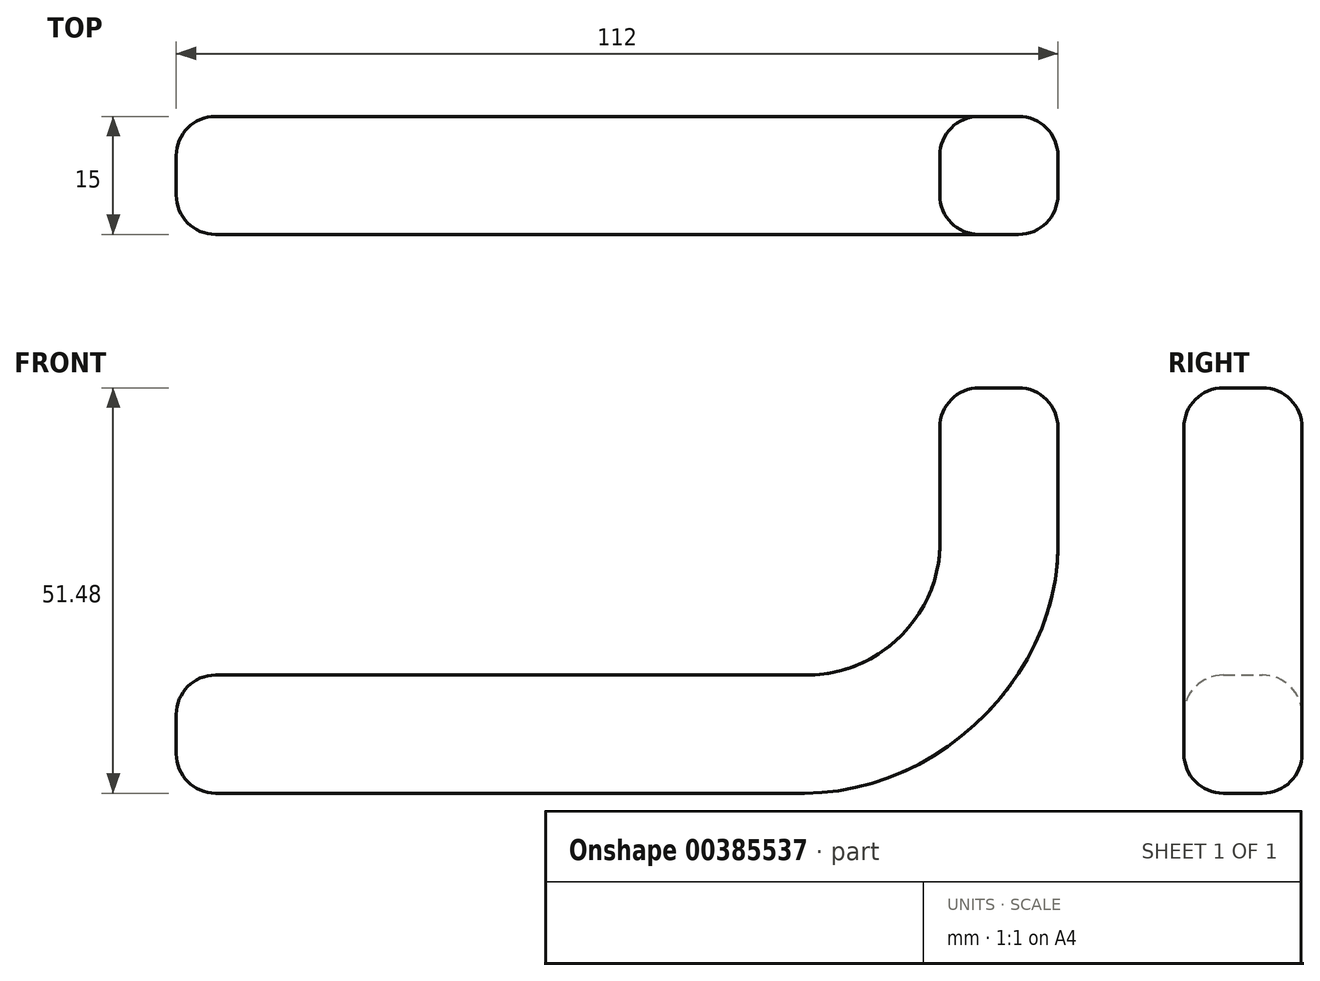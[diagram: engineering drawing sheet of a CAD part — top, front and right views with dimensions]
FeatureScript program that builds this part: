
annotation { "Feature Type Name" : "Feature", "Feature Type Description" : "" }
export const myFeature = defineFeature(function(context is Context, id is Id, definition is map)
    precondition{}
    {
        {
            var Q0;
            Q0=qCreatedBy(makeId("Front.planeOp"),FACE);
            var sketch = newSketch(context, id + "F0", { "sketchPlane" : qUnion([Q0])});
            skLineSegment(sketch, "E0", {"start": v(0, 15) * mm, "end": v(80, 15) * mm});
            skLineSegment(sketch, "E1.1", {"start": v(-0.18, 0) * mm, "end": v(79.82, 0) * mm});
            skLineSegment(sketch, "E2.bottom", {"start": v(97, 31.48) * mm, "end": v(112, 31.48) * mm});
            skLineSegment(sketch, "E2.top", {"start": v(97, 51.48) * mm, "end": v(112, 51.48) * mm});
            skLineSegment(sketch, "E2.left", {"start": v(97, 31.48) * mm, "end": v(97, 51.48) * mm});
            skLineSegment(sketch, "E2.right", {"start": v(112, 31.48) * mm, "end": v(112, 51.48) * mm});
            skFitSpline(sketch, "E3", {"points": [v(80, 15) * mm, v(97, 31.48) * mm], "startDerivative": vector(30.17, 0) * mm, "endDerivative": vector(0, 24.3) * mm});
            skFitSpline(sketch, "E4", {"points": [v(112, 31.48) * mm, v(79.82, 0) * mm], "startDerivative": vector(0, -49.43) * mm, "endDerivative": vector(-51.52, 0) * mm});
            skLineSegment(sketch, "E5", {"start": v(80, 15) * mm, "end": v(79.82, 0) * mm});
            skLineSegment(sketch, "E6", {"start": v(0, 15) * mm, "end": v(-0.18, 0) * mm});
            skLineSegment(sketch, "E7.left", {"start": v(0, 15) * mm, "end": v(0, 0) * mm});
            skSolve(sketch);
        }
        {
            var Q0;
            Q0=makeQuery(id+"F0.imprint","IMPRINT",FACE,{"disambiguationData":[TD([[makeQuery(id+"F0.imprint","IMPRINT",EDGE,{"derivedFrom":sQuery(id+"F0.wireOp",EDGE,"meLjfQBB-0KZx-YIKJ-ggGc-JeM5xshYHCOn.bottom")}),-1.0]])]});
            var Q1;
            Q1=makeQuery(id+"F0.imprint","IMPRINT",FACE,{"disambiguationData":[TD([[makeQuery(id+"F0.imprint","IMPRINT",EDGE,{"derivedFrom":sQuery(id+"F0.wireOp",EDGE,"meLjfQBB-0KZx-YIKJ-ggGc-JeM5xshYHCOn.right")}),1.0]])]});
            var Q2;
            Q2=makeQuery(id+"F0.imprint","IMPRINT",FACE,{"disambiguationData":[TD([[makeQuery(id+"F0.imprint","IMPRINT",EDGE,{"derivedFrom":sQuery(id+"F0.wireOp",EDGE,"E2.bottom")}),-1.0]])]});
            var Q3;
            Q3=makeQuery(id+"F0.imprint","IMPRINT",FACE,{"disambiguationData":[TD([[makeQuery(id+"F0.imprint","IMPRINT",EDGE,{"derivedFrom":sQuery(id+"F0.wireOp",EDGE,"E2.bottom")}),1.0]])]});
            var Q4;
            Q4=makeQuery(id+"F0.imprint","IMPRINT",FACE,{"disambiguationData":[TD([[makeQuery(id+"F0.imprint","IMPRINT",EDGE,{"derivedFrom":sQuery(id+"F0.wireOp",EDGE,"E0")}),-1.0]])]});
            var Q5;
            Q5=makeQuery(id+"F0.imprint","IMPRINT",FACE,{"disambiguationData":[TD([[makeQuery(id+"F0.imprint","IMPRINT",EDGE,{"derivedFrom":sQuery(id+"F0.wireOp",EDGE,"E7.bottom")}),1.0]])]});
            extrude(context, id + "F1", {"entities" : qUnion([Q0, Q1, Q2, Q3, Q4, Q5]), "depth" : 15 * mm});
        }
        {
            var Q0;
            Q0=makeQuery(id+"F1.opExtrude","SWEPT_FACE",FACE,{"disambiguationData":[OSD([sQuery(id+"F0.wireOp",EDGE,"E0"),sQuery(id+"F0.wireOp",EDGE,"E7.bottom")])]});
            var Q1;
            Q1=makeQuery(id+"F1.opExtrude","SWEPT_FACE",FACE,{"disambiguationData":[OSD([sQuery(id+"F0.wireOp",EDGE,"E2.top")])]});
            var Q2;
            Q2=makeQuery(id+"F1.opExtrude","CAP_FACE",FACE,{"disambiguationData":[OSD([sQuery(id+"F0.wireOp",EDGE,"E0"),sQuery(id+"F0.wireOp",EDGE,"E1.1"),sQuery(id+"F0.wireOp",EDGE,"E2.top"),sQuery(id+"F0.wireOp",EDGE,"E2.left"),sQuery(id+"F0.wireOp",EDGE,"E2.right"),sQuery(id+"F0.wireOp",EDGE,"E3"),sQuery(id+"F0.wireOp",EDGE,"E4"),sQuery(id+"F0.wireOp",EDGE,"E7.bottom"),sQuery(id+"F0.wireOp",EDGE,"E7.top"),sQuery(id+"F0.wireOp",EDGE,"E7.right")])],"isStart":false});
            var Q3;
            Q3=makeQuery(id+"F1.opExtrude","SWEPT_FACE",FACE,{"disambiguationData":[OSD([sQuery(id+"F0.wireOp",EDGE,"E2.right")])]});
            var Q4;
            Q4=makeQuery(id+"F1.opExtrude","SWEPT_FACE",FACE,{"disambiguationData":[OSD([sQuery(id+"F0.wireOp",EDGE,"E4")])]});
            var Q5;
            Q5=makeQuery(id+"F1.opExtrude","SWEPT_FACE",FACE,{"disambiguationData":[OSD([sQuery(id+"F0.wireOp",EDGE,"E1.1"),sQuery(id+"F0.wireOp",EDGE,"E7.top")])]});
            fillet(context, id + "F2", {"entities" : qUnion([Q0, Q1, Q2, Q3, Q4, Q5]), "radius" : 5 * mm, "tangentPropagation" : true, "allowEdgeOverflow" : false});
        }
        {
            var Q0;
            Q0=makeQuery(id+"F1.opExtrude","SWEPT_FACE",FACE,{"disambiguationData":[OSD([sQuery(id+"F0.wireOp",EDGE,"E1.1")])]});
            var Q1;
            {var subQ0=sQuery(id+"F0.wireOp",EDGE,"E1.1");Q1=makeQuery(id+"F2.opFillet","BLEND_FACE",FACE,{"disambiguationData":[OSD([subQ0]),TDD([makeQuery(id+"F1.opExtrude","CAP_EDGE",EDGE,{"disambiguationData":[OSD([subQ0])],"isStart":false})])]});}
            var Q2;
            {var subQ0=sQuery(id+"F0.wireOp",EDGE,"E1.1");Q2=makeQuery(id+"F2.opFillet","BLEND_FACE",FACE,{"disambiguationData":[OSD([subQ0]),TDD([makeQuery(id+"F1.opExtrude","CAP_EDGE",EDGE,{"disambiguationData":[OSD([subQ0])],"isStart":true})])]});}
            var Q3;
            {var subQ0=sQuery(id+"F0.wireOp",EDGE,"E7.left");var subQ1=sQuery(id+"F0.wireOp",EDGE,"E6");var subQ2=sQuery(id+"F0.wireOp",EDGE,"E0");Q3=makeQuery(id+"F2.opFillet","BLEND_FACE",FACE,{"disambiguationData":[OSD([subQ2,subQ1,subQ0]),TDD([makeQuery(id+"F1.opExtrude","SWEPT_EDGE",EDGE,{"disambiguationData":[OSD([subQ2,subQ1,subQ0])]})])]});}
            var Q4;
            {var subQ0=sQuery(id+"F0.wireOp",EDGE,"E7.left");var subQ1=sQuery(id+"F0.wireOp",EDGE,"E1.1");Q4=makeQuery(id+"F2.opFillet","BLEND_FACE",FACE,{"disambiguationData":[OSD([subQ1,subQ0]),TDD([makeQuery(id+"F1.opExtrude","CAP_VERTEX",VERTEX,{"disambiguationData":[OSD([subQ1,subQ0])],"isStart":false})])]});}
            var Q5;
            Q5=makeQuery(id+"F2.opFillet","BLEND_FACE",FACE,{"disambiguationData":[OSD([sQuery(id+"F0.wireOp",EDGE,"E7.left")])]});
            var Q6;
            {var subQ0=sQuery(id+"F0.wireOp",EDGE,"E7.left");Q6=makeQuery(id+"F2.opFillet","BLEND_EDGE",EDGE,{"blendedFrom":[makeQuery(id+"F1.opExtrude","SWEPT_EDGE",EDGE,{"disambiguationData":[OSD([sQuery(id+"F0.wireOp",EDGE,"E0"),sQuery(id+"F0.wireOp",EDGE,"E6"),subQ0])]}),makeQuery(id+"F1.opExtrude","SWEPT_FACE",FACE,{"disambiguationData":[OSD([subQ0])]})],"blendedInto":[makeQuery(id+"F1.opExtrude","SWEPT_FACE",FACE,{"disambiguationData":[OSD([subQ0])]})]});}
            var Q7;
            {var subQ0=sQuery(id+"F0.wireOp",EDGE,"E0");Q7=makeQuery(id+"F2.opFillet","BLEND_FACE",FACE,{"disambiguationData":[OSD([subQ0]),TDD([makeQuery(id+"F1.opExtrude","CAP_EDGE",EDGE,{"disambiguationData":[OSD([subQ0])],"isStart":true})])]});}
            var Q8;
            {var subQ0=sQuery(id+"F0.wireOp",EDGE,"E0");Q8=makeQuery(id+"F2.opFillet","BLEND_EDGE",EDGE,{"blendedFrom":[makeQuery(id+"F1.opExtrude","CAP_EDGE",EDGE,{"disambiguationData":[OSD([subQ0])],"isStart":true}),makeQuery(id+"F1.opExtrude","SWEPT_FACE",FACE,{"disambiguationData":[OSD([subQ0])]})],"blendedInto":[makeQuery(id+"F1.opExtrude","SWEPT_FACE",FACE,{"disambiguationData":[OSD([subQ0])]})]});}
            var Q9;
            Q9=makeQuery(id+"F1.opExtrude","SWEPT_FACE",FACE,{"disambiguationData":[OSD([sQuery(id+"F0.wireOp",EDGE,"E0")])]});
            var Q10;
            {var subQ0=sQuery(id+"F0.wireOp",EDGE,"E0");Q10=makeQuery(id+"F2.opFillet","BLEND_FACE",FACE,{"disambiguationData":[OSD([subQ0]),TDD([makeQuery(id+"F1.opExtrude","CAP_EDGE",EDGE,{"disambiguationData":[OSD([subQ0])],"isStart":false})])]});}
            var Q11;
            {var subQ0=sQuery(id+"F0.wireOp",EDGE,"E3");Q11=makeQuery(id+"F2.opFillet","BLEND_FACE",FACE,{"disambiguationData":[OSD([subQ0]),TDD([makeQuery(id+"F1.opExtrude","CAP_EDGE",EDGE,{"disambiguationData":[OSD([subQ0])],"isStart":false})])]});}
            var Q12;
            Q12=makeQuery(id+"F1.opExtrude","CAP_FACE",FACE,{"disambiguationData":[OSD([sQuery(id+"F0.wireOp",EDGE,"E0"),sQuery(id+"F0.wireOp",EDGE,"E1.1"),sQuery(id+"F0.wireOp",EDGE,"E2.top"),sQuery(id+"F0.wireOp",EDGE,"E2.left"),sQuery(id+"F0.wireOp",EDGE,"E2.right"),sQuery(id+"F0.wireOp",EDGE,"E3"),sQuery(id+"F0.wireOp",EDGE,"E4"),sQuery(id+"F0.wireOp",EDGE,"E7.left")])],"isStart":false});
            var Q13;
            {var subQ0=sQuery(id+"F0.wireOp",EDGE,"E4");Q13=makeQuery(id+"F2.opFillet","BLEND_FACE",FACE,{"disambiguationData":[OSD([subQ0]),TDD([makeQuery(id+"F1.opExtrude","CAP_EDGE",EDGE,{"disambiguationData":[OSD([subQ0])],"isStart":false})])]});}
            var Q14;
            {var subQ0=sQuery(id+"F0.wireOp",EDGE,"E2.right");Q14=makeQuery(id+"F2.opFillet","BLEND_FACE",FACE,{"disambiguationData":[OSD([subQ0]),TDD([makeQuery(id+"F1.opExtrude","CAP_EDGE",EDGE,{"disambiguationData":[OSD([subQ0])],"isStart":false})])]});}
            var Q15;
            {var subQ0=sQuery(id+"F0.wireOp",EDGE,"E2.left");Q15=makeQuery(id+"F2.opFillet","BLEND_FACE",FACE,{"disambiguationData":[OSD([subQ0]),TDD([makeQuery(id+"F1.opExtrude","CAP_EDGE",EDGE,{"disambiguationData":[OSD([subQ0])],"isStart":false})])]});}
            var Q16;
            {var subQ0=sQuery(id+"F0.wireOp",EDGE,"E2.top");Q16=makeQuery(id+"F2.opFillet","BLEND_EDGE",EDGE,{"blendedFrom":[makeQuery(id+"F1.opExtrude","CAP_VERTEX",VERTEX,{"disambiguationData":[OSD([subQ0,sQuery(id+"F0.wireOp",EDGE,"E2.left")])],"isStart":false}),makeQuery(id+"F1.opExtrude","CAP_EDGE",EDGE,{"disambiguationData":[OSD([subQ0])],"isStart":false})],"blendedInto":[]});}
            var Q17;
            {var subQ0=sQuery(id+"F0.wireOp",EDGE,"E2.top");Q17=makeQuery(id+"F2.opFillet","BLEND_FACE",FACE,{"disambiguationData":[OSD([subQ0]),TDD([makeQuery(id+"F1.opExtrude","CAP_EDGE",EDGE,{"disambiguationData":[OSD([subQ0])],"isStart":false})])]});}
            var Q18;
            {var subQ0=sQuery(id+"F0.wireOp",EDGE,"E2.right");var subQ1=sQuery(id+"F0.wireOp",EDGE,"E2.top");Q18=makeQuery(id+"F2.opFillet","BLEND_FACE",FACE,{"disambiguationData":[OSD([subQ1,subQ0]),TDD([makeQuery(id+"F1.opExtrude","CAP_VERTEX",VERTEX,{"disambiguationData":[OSD([subQ1,subQ0])],"isStart":false})])]});}
            var Q19;
            {var subQ0=sQuery(id+"F0.wireOp",EDGE,"E3");Q19=makeQuery(id+"F2.opFillet","BLEND_FACE",FACE,{"disambiguationData":[OSD([subQ0]),TDD([makeQuery(id+"F1.opExtrude","CAP_EDGE",EDGE,{"disambiguationData":[OSD([subQ0])],"isStart":true})])]});}
            var Q20;
            Q20=makeQuery(id+"F1.opExtrude","SWEPT_FACE",FACE,{"disambiguationData":[OSD([sQuery(id+"F0.wireOp",EDGE,"E3")])]});
            var Q21;
            {var subQ0=sQuery(id+"F0.wireOp",EDGE,"E4");Q21=makeQuery(id+"F2.opFillet","BLEND_EDGE",EDGE,{"blendedFrom":[makeQuery(id+"F1.opExtrude","CAP_EDGE",EDGE,{"disambiguationData":[OSD([subQ0])],"isStart":true}),makeQuery(id+"F1.opExtrude","CAP_FACE",FACE,{"disambiguationData":[OSD([sQuery(id+"F0.wireOp",EDGE,"E0"),sQuery(id+"F0.wireOp",EDGE,"E1.1"),sQuery(id+"F0.wireOp",EDGE,"E2.top"),sQuery(id+"F0.wireOp",EDGE,"E2.left"),sQuery(id+"F0.wireOp",EDGE,"E2.right"),sQuery(id+"F0.wireOp",EDGE,"E3"),subQ0,sQuery(id+"F0.wireOp",EDGE,"E7.left")])],"isStart":true})],"blendedInto":[makeQuery(id+"F1.opExtrude","CAP_FACE",FACE,{"disambiguationData":[OSD([sQuery(id+"F0.wireOp",EDGE,"E0"),sQuery(id+"F0.wireOp",EDGE,"E1.1"),sQuery(id+"F0.wireOp",EDGE,"E2.top"),sQuery(id+"F0.wireOp",EDGE,"E2.left"),sQuery(id+"F0.wireOp",EDGE,"E2.right"),sQuery(id+"F0.wireOp",EDGE,"E3"),subQ0,sQuery(id+"F0.wireOp",EDGE,"E7.left")])],"isStart":true})]});}
            var Q22;
            Q22=makeQuery(id+"F1.opExtrude","CAP_FACE",FACE,{"disambiguationData":[OSD([sQuery(id+"F0.wireOp",EDGE,"E0"),sQuery(id+"F0.wireOp",EDGE,"E1.1"),sQuery(id+"F0.wireOp",EDGE,"E2.top"),sQuery(id+"F0.wireOp",EDGE,"E2.left"),sQuery(id+"F0.wireOp",EDGE,"E2.right"),sQuery(id+"F0.wireOp",EDGE,"E3"),sQuery(id+"F0.wireOp",EDGE,"E4"),sQuery(id+"F0.wireOp",EDGE,"E7.left")])],"isStart":true});
            var Q23;
            {var subQ0=sQuery(id+"F0.wireOp",EDGE,"E2.left");Q23=makeQuery(id+"F2.opFillet","BLEND_FACE",FACE,{"disambiguationData":[OSD([subQ0]),TDD([makeQuery(id+"F1.opExtrude","CAP_EDGE",EDGE,{"disambiguationData":[OSD([subQ0])],"isStart":true})])]});}
            var Q24;
            {var subQ0=sQuery(id+"F0.wireOp",EDGE,"E2.left");var subQ1=sQuery(id+"F0.wireOp",EDGE,"E2.top");Q24=makeQuery(id+"F2.opFillet","BLEND_FACE",FACE,{"disambiguationData":[OSD([subQ1,subQ0]),TDD([makeQuery(id+"F1.opExtrude","CAP_VERTEX",VERTEX,{"disambiguationData":[OSD([subQ1,subQ0])],"isStart":true})])]});}
            var Q25;
            {var subQ0=sQuery(id+"F0.wireOp",EDGE,"E2.left");var subQ1=sQuery(id+"F0.wireOp",EDGE,"E2.top");Q25=makeQuery(id+"F2.opFillet","BLEND_FACE",FACE,{"disambiguationData":[OSD([subQ1,subQ0]),TDD([makeQuery(id+"F1.opExtrude","SWEPT_EDGE",EDGE,{"disambiguationData":[OSD([subQ1,subQ0])]})])]});}
            var Q26;
            {var subQ0=sQuery(id+"F0.wireOp",EDGE,"E2.left");var subQ1=sQuery(id+"F0.wireOp",EDGE,"E2.top");Q26=makeQuery(id+"F2.opFillet","BLEND_EDGE",EDGE,{"blendedFrom":[makeQuery(id+"F1.opExtrude","CAP_VERTEX",VERTEX,{"disambiguationData":[OSD([subQ1,subQ0])],"isStart":false}),makeQuery(id+"F1.opExtrude","SWEPT_EDGE",EDGE,{"disambiguationData":[OSD([subQ1,subQ0])]})],"blendedInto":[]});}
            var Q27;
            {var subQ0=sQuery(id+"F0.wireOp",EDGE,"E2.top");Q27=makeQuery(id+"F2.opFillet","BLEND_FACE",FACE,{"disambiguationData":[OSD([subQ0]),TDD([makeQuery(id+"F1.opExtrude","CAP_EDGE",EDGE,{"disambiguationData":[OSD([subQ0])],"isStart":true})])]});}
            var Q28;
            Q28=makeQuery(id+"F1.opExtrude","SWEPT_FACE",FACE,{"disambiguationData":[OSD([sQuery(id+"F0.wireOp",EDGE,"E2.top")])]});
            var Q29;
            {var subQ0=sQuery(id+"F0.wireOp",EDGE,"E2.right");var subQ1=sQuery(id+"F0.wireOp",EDGE,"E2.top");Q29=makeQuery(id+"F2.opFillet","BLEND_FACE",FACE,{"disambiguationData":[OSD([subQ1,subQ0]),TDD([makeQuery(id+"F1.opExtrude","SWEPT_EDGE",EDGE,{"disambiguationData":[OSD([subQ1,subQ0])]})])]});}
            var Q30;
            {var subQ0=sQuery(id+"F0.wireOp",EDGE,"E2.right");var subQ1=sQuery(id+"F0.wireOp",EDGE,"E2.top");Q30=makeQuery(id+"F2.opFillet","BLEND_FACE",FACE,{"disambiguationData":[OSD([subQ1,subQ0]),TDD([makeQuery(id+"F1.opExtrude","CAP_VERTEX",VERTEX,{"disambiguationData":[OSD([subQ1,subQ0])],"isStart":true})])]});}
            var Q31;
            {var subQ0=sQuery(id+"F0.wireOp",EDGE,"E2.right");Q31=makeQuery(id+"F2.opFillet","BLEND_FACE",FACE,{"disambiguationData":[OSD([subQ0]),TDD([makeQuery(id+"F1.opExtrude","CAP_EDGE",EDGE,{"disambiguationData":[OSD([subQ0])],"isStart":true})])]});}
            var Q32;
            {var subQ0=sQuery(id+"F0.wireOp",EDGE,"E4");Q32=makeQuery(id+"F2.opFillet","BLEND_FACE",FACE,{"disambiguationData":[OSD([subQ0]),TDD([makeQuery(id+"F1.opExtrude","CAP_EDGE",EDGE,{"disambiguationData":[OSD([subQ0])],"isStart":true})])]});}
            var Q33;
            {var subQ0=sQuery(id+"F0.wireOp",EDGE,"E4");Q33=makeQuery(id+"F2.opFillet","BLEND_EDGE",EDGE,{"blendedFrom":[makeQuery(id+"F1.opExtrude","CAP_EDGE",EDGE,{"disambiguationData":[OSD([subQ0])],"isStart":true}),makeQuery(id+"F1.opExtrude","SWEPT_FACE",FACE,{"disambiguationData":[OSD([subQ0])]})],"blendedInto":[makeQuery(id+"F1.opExtrude","SWEPT_FACE",FACE,{"disambiguationData":[OSD([subQ0])]})]});}
            fillet(context, id + "F3", {"entities" : qUnion([Q0, Q1, Q2, Q3, Q4, Q5, Q6, Q7, Q8, Q9, Q10, Q11, Q12, Q13, Q14, Q15, Q16, Q17, Q18, Q19, Q20, Q21, Q22, Q23, Q24, Q25, Q26, Q27, Q28, Q29, Q30, Q31, Q32, Q33]), "radius" : 5 * mm, "tangentPropagation" : true, "allowEdgeOverflow" : false});
        }
    });
